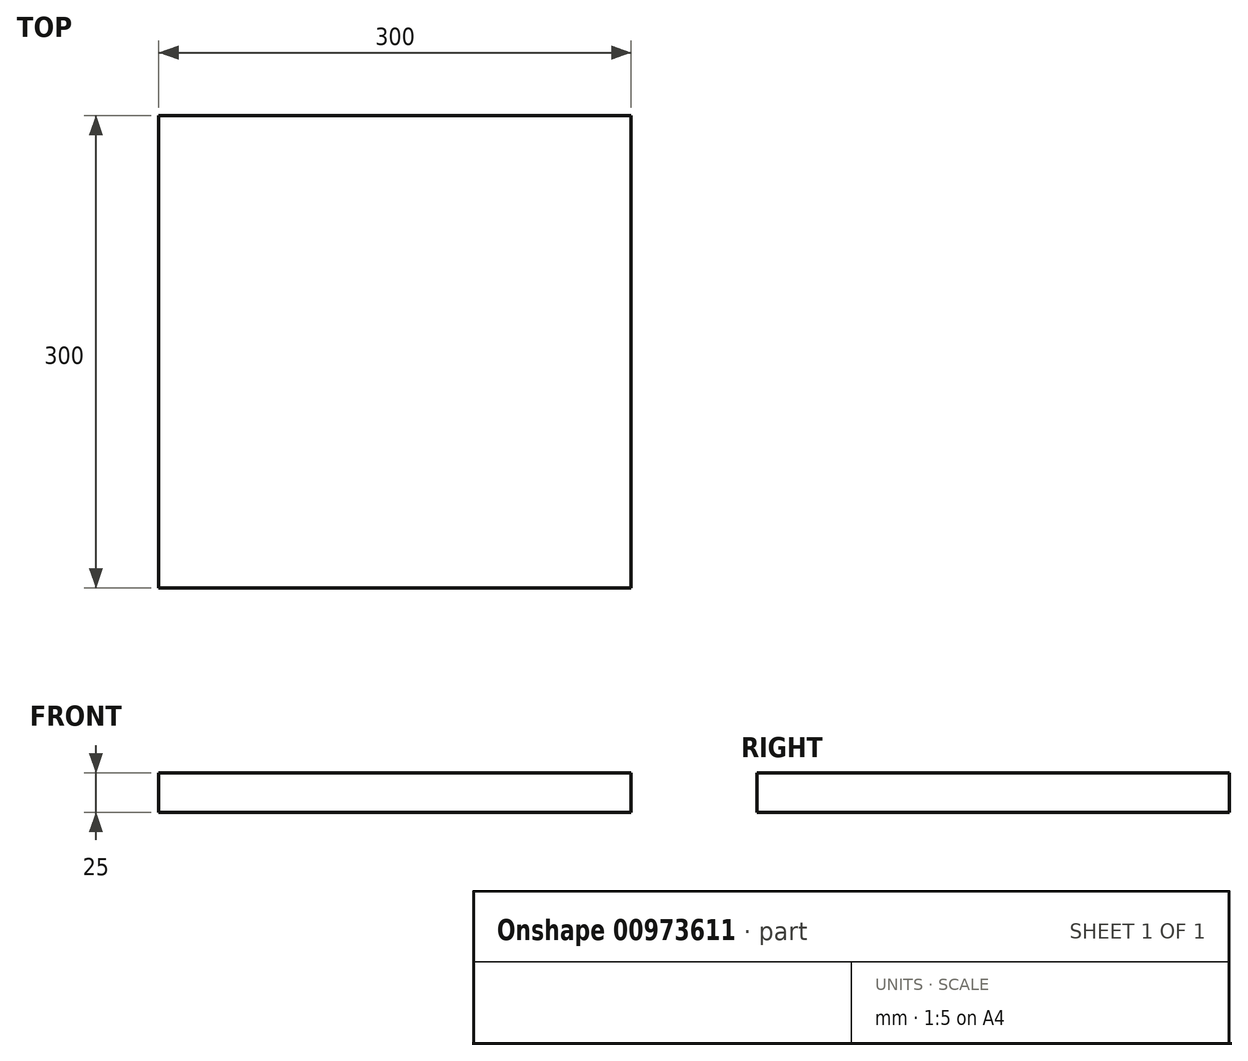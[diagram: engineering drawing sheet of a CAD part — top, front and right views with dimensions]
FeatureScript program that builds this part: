
annotation { "Feature Type Name" : "Feature", "Feature Type Description" : "" }
export const myFeature = defineFeature(function(context is Context, id is Id, definition is map)
    precondition{}
    {
        {
            var Q0;
            Q0=qCreatedBy(makeId("Top.planeOp"),FACE);
            var sketch = newSketch(context, id + "F0", { "sketchPlane" : qUnion([Q0])});
            skLineSegment(sketch, "E0.bottom", {"start": v(150, 150) * mm, "end": v(-150, 150) * mm});
            skLineSegment(sketch, "E0.top", {"start": v(150, -150) * mm, "end": v(-150, -150) * mm});
            skLineSegment(sketch, "E0.left", {"start": v(150, 150) * mm, "end": v(150, -150) * mm});
            skLineSegment(sketch, "E0.right", {"start": v(-150, 150) * mm, "end": v(-150, -150) * mm});
            skPoint(sketch, "E0.middle", {"position": v(0, 0) * mm});
            skSolve(sketch);
        }
        {
            var Q0;
            Q0 = qSketchRegion(id + "F0", true);
            extrude(context, id + "F1", {"entities" : qUnion([Q0]), "depth" : 25 * mm, "offsetDistance" : 25 * mm});
        }
    });
